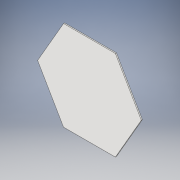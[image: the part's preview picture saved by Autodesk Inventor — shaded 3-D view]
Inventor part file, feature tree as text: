
AUTODESK INVENTOR PART (.ipt)
format: ipt  version: 2019 (Build 230136000, 136)  size: 104,448 bytes
history: native  units: mm
features: sketch x2, extrude x1, projected_geometry x1
ambient origin geometry x8: Origin, YZ Plane, XZ Plane, XY Plane, X Axis, Y Axis, Z Axis, Center Point
bodies: Solid1 (feature_tree)
feature tree (4):
  extrude  "Extrusion1"  Depth=2.0mm TaperAngle=0.0deg
  sketch  "Sketch3"  dims[d3=191.680289mm d4=166.0mm]
  sketch  "Sketch1"  dims[d0=166.0mm d1=2.0mm d2=0.0mm]
  projected_geometry  "Projected Loop1"
